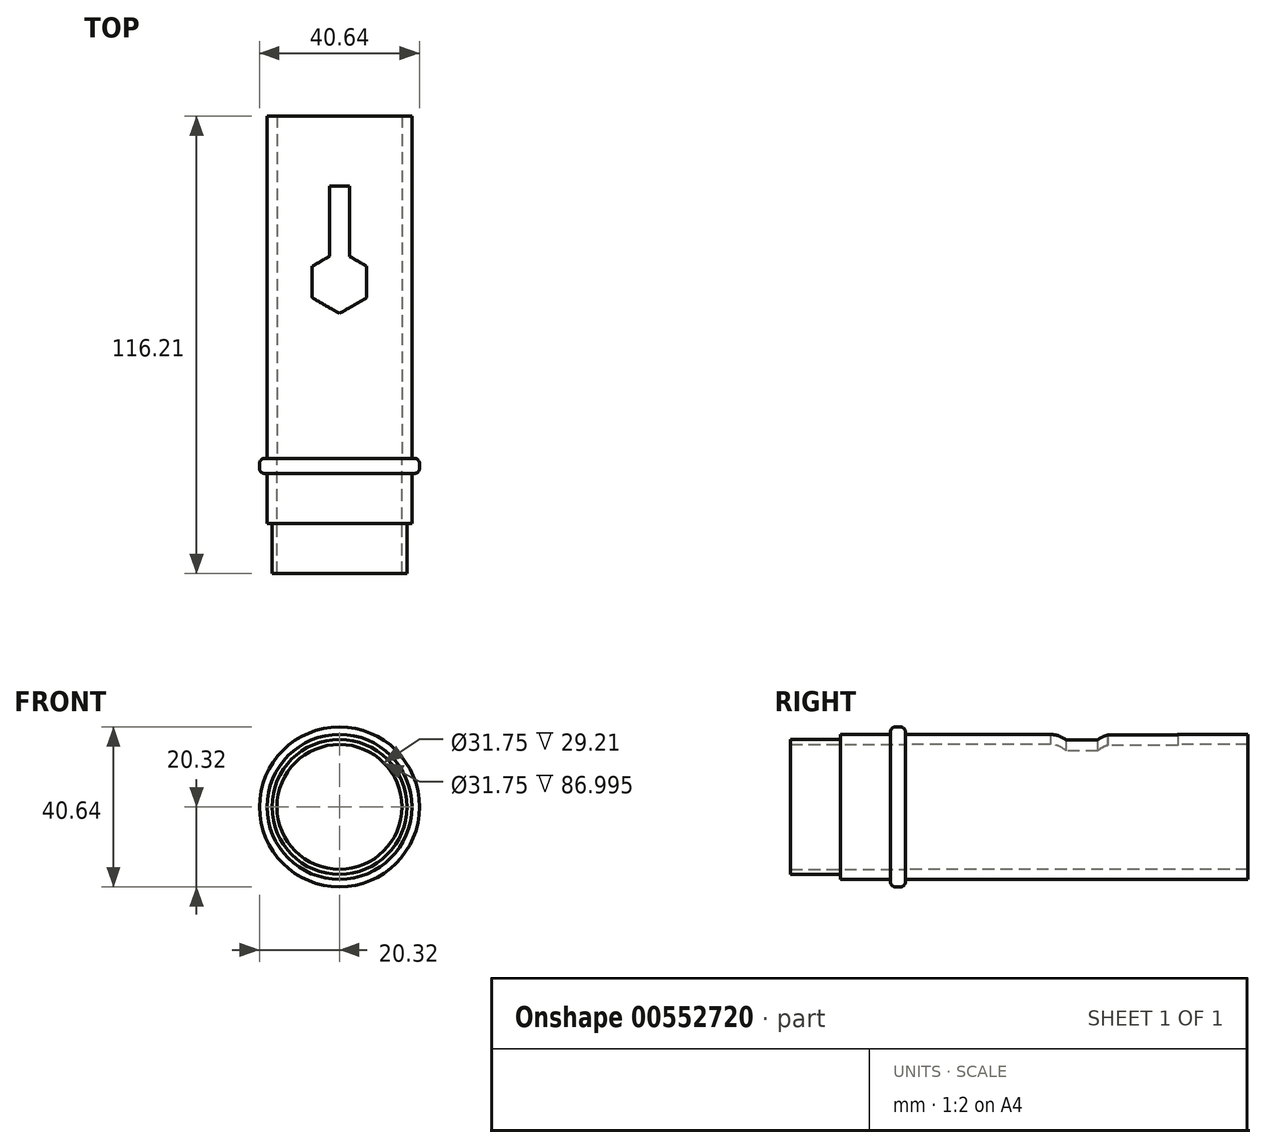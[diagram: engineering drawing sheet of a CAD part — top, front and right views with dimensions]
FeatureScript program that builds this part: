
annotation { "Feature Type Name" : "Feature", "Feature Type Description" : "" }
export const myFeature = defineFeature(function(context is Context, id is Id, definition is map)
    precondition{}
    {
        {
            var Q0;
            Q0=qCreatedBy(makeId("Front.planeOp"),FACE);
            var sketch = newSketch(context, id + "F0", { "sketchPlane" : qUnion([Q0])});
            skCircle(sketch, "E0", {"center": v(0, 0) * mm, "radius": 15.88 * mm});
            skCircle(sketch, "E1", {"center": v(0, 0) * mm, "radius": 20.32 * mm});
            skSolve(sketch);
        }
        {
            var Q0;
            Q0 = qSketchRegion(id + "F0", true);
            extrude(context, id + "F1", {"entities" : qUnion([Q0]), "endBound" : BoundingType.SYMMETRIC, "depth" : 3.8 * mm, "offsetDistance" : 25.4 * mm});
        }
        {
            var Q0;
            Q0=makeQuery(id+"F1.opExtrude","SWEPT_FACE",FACE,{"disambiguationData":[OSD([sQuery(id+"F0.wireOp",EDGE,"E1")])]});
            fillet(context, id + "F2", {"entities" : qUnion([Q0]), "radius" : 1.27 * mm, "tangentPropagation" : true, "allowEdgeOverflow" : false});
        }
        {
            var Q0;
            Q0=qCreatedBy(makeId("Front.planeOp"),FACE);
            var sketch = newSketch(context, id + "F3", { "sketchPlane" : qUnion([Q0])});
            skCircle(sketch, "E2", {"center": v(0, 0) * mm, "radius": 15.88 * mm});
            skCircle(sketch, "E3", {"center": v(0, 0) * mm, "radius": 18.41 * mm});
            skSolve(sketch);
        }
        {
            var Q0;
            Q0=qSketchRegion(id+"F3",true);
            extrude(context, id + "F4", {"entities" : qUnion([Q0]), "operationType" : NewBodyOperationType.ADD, "depth" : 14.6 * mm, "offsetDistance" : 25.4 * mm});
        }
        {
            var Q0;
            Q0=qCreatedBy(makeId("Front.planeOp"),FACE);
            var sketch = newSketch(context, id + "F5", { "sketchPlane" : qUnion([Q0])});
            skCircle(sketch, "E4", {"center": v(0, 0) * mm, "radius": 17.15 * mm});
            skCircle(sketch, "E5", {"center": v(0, 0) * mm, "radius": 15.88 * mm});
            skSolve(sketch);
        }
        {
            var Q0;
            Q0 = qSketchRegion(id + "F5", true);
            extrude(context, id + "F6", {"entities" : qUnion([Q0]), "operationType" : NewBodyOperationType.ADD, "depth" : 27.3 * mm, "offsetDistance" : 25.4 * mm, "hasSecondDirection" : true, "secondDirectionOppositeDirection" : false, "secondDirectionDepth" : 14.6 * mm});
        }
        {
            var Q0;
            Q0=qCreatedBy(makeId("Front.planeOp"),FACE);
            var sketch = newSketch(context, id + "F7", { "sketchPlane" : qUnion([Q0])});
            skCircle(sketch, "E6", {"center": v(0, 0) * mm, "radius": 18.41 * mm});
            skCircle(sketch, "E7", {"center": v(0, 0) * mm, "radius": 15.88 * mm});
            skSolve(sketch);
        }
        {
            var Q0;
            Q0 = qSketchRegion(id + "F7", true);
            extrude(context, id + "F8", {"entities" : qUnion([Q0]), "oppositeDirection" : true, "depth" : 88.9 * mm, "offsetDistance" : 25.4 * mm, "hasSecondDirection" : true, "secondDirectionOppositeDirection" : true, "secondDirectionDepth" : 1.9 * mm});
        }
        {
            var Q0;
            Q0=qCreatedBy(makeId("Top.planeOp"),FACE);
            var sketch = newSketch(context, id + "F9", { "sketchPlane" : qUnion([Q0])});
            skCircle(sketch, "E8.cCircle", {"center": v(0, 46.74) * mm, "radius": 8 * mm, "construction": true});
            skLineSegment(sketch, "E8.0", {"start": v(0, 38.73) * mm, "end": v(-6.93, 42.74) * mm});
            skLineSegment(sketch, "E8.1", {"start": v(-6.93, 42.74) * mm, "end": v(-6.93, 50.74) * mm});
            skLineSegment(sketch, "E8.2", {"start": v(-6.93, 50.74) * mm, "end": v(0, 54.74) * mm});
            skLineSegment(sketch, "E8.3", {"start": v(0, 54.74) * mm, "end": v(6.93, 50.74) * mm});
            skLineSegment(sketch, "E8.4", {"start": v(6.93, 50.74) * mm, "end": v(6.93, 42.74) * mm});
            skLineSegment(sketch, "E8.5", {"start": v(6.93, 42.74) * mm, "end": v(0, 38.73) * mm});
            skSolve(sketch);
        }
        {
            var Q0;
            Q0=qCreatedBy(makeId("Top.planeOp"),FACE);
            var sketch = newSketch(context, id + "F10", { "sketchPlane" : qUnion([Q0])});
            skLineSegment(sketch, "E9.bottom", {"start": v(-2.49, 71.12) * mm, "end": v(2.6, 71.12) * mm});
            skLineSegment(sketch, "E9.top", {"start": v(-2.49, 50.8) * mm, "end": v(2.6, 50.8) * mm});
            skLineSegment(sketch, "E9.left", {"start": v(-2.49, 71.12) * mm, "end": v(-2.49, 50.8) * mm});
            skLineSegment(sketch, "E9.right", {"start": v(2.6, 71.12) * mm, "end": v(2.6, 50.8) * mm});
            skSolve(sketch);
        }
        {
            var Q0;
            Q0 = qSketchRegion(id + "F9", true);
            var Q1;
            Q1 = qSketchRegion(id + "F10", true);
            extrude(context, id + "F11", {"entities" : qUnion([Q0, Q1]), "operationType" : NewBodyOperationType.REMOVE, "depth" : 25.4 * mm, "offsetDistance" : 25.4 * mm});
        }
    });
